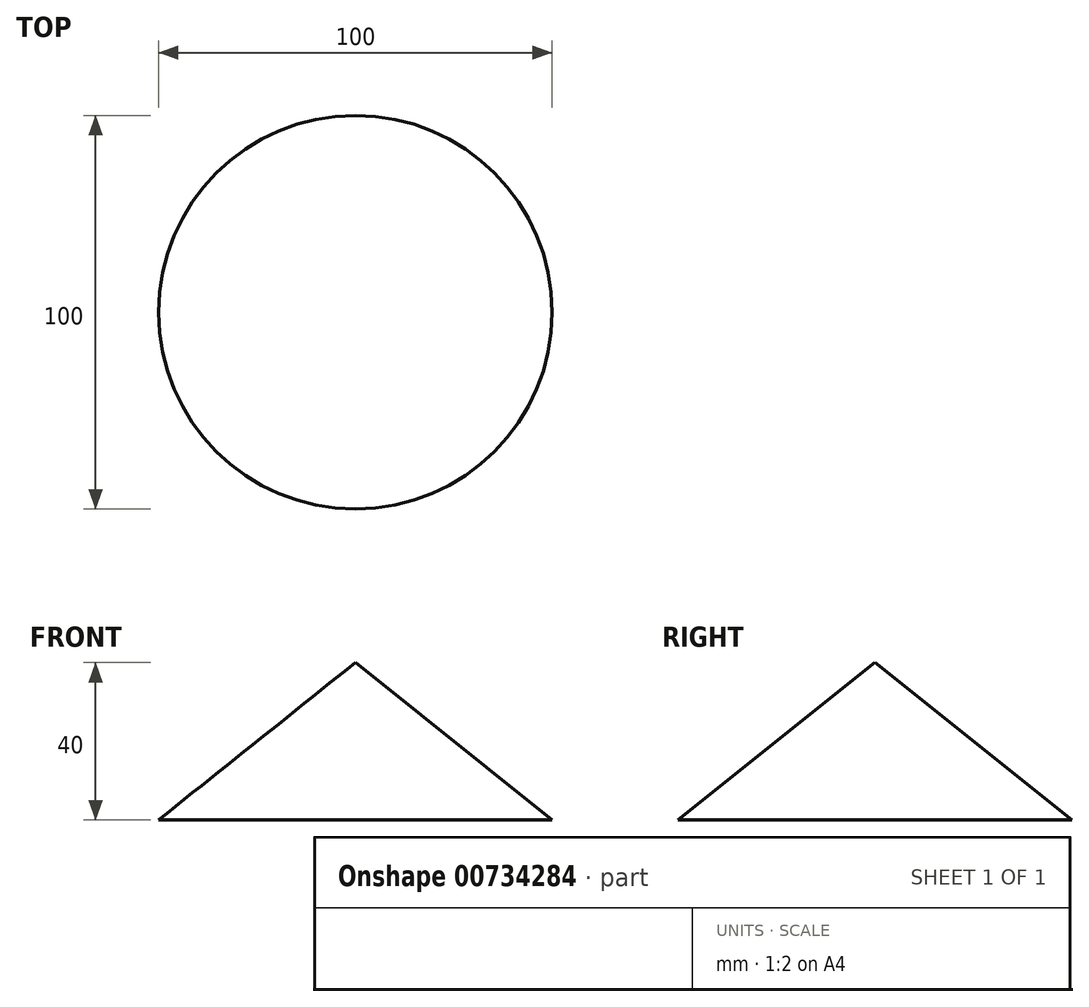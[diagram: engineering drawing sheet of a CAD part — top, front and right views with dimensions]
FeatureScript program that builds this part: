
annotation { "Feature Type Name" : "Feature", "Feature Type Description" : "" }
export const myFeature = defineFeature(function(context is Context, id is Id, definition is map)
    precondition{}
    {
        {
            var Q0;
            Q0=qCreatedBy(makeId("Front.planeOp"),FACE);
            var sketch = newSketch(context, id + "F0", { "sketchPlane" : qUnion([Q0])});
            skLineSegment(sketch, "E0", {"start": v(0, 0) * mm, "end": v(0, 40) * mm});
            skLineSegment(sketch, "E1", {"start": v(0, 40) * mm, "end": v(50, 0) * mm});
            skLineSegment(sketch, "E2", {"start": v(50, 0) * mm, "end": v(0, 0) * mm});
            skSolve(sketch);
        }
        {
            var Q0;
            Q0 = qSketchRegion(id + "F0", true);
            var Q1;
            Q1=makeQuery(id+"F0.imprint","IMPRINT",FACE,{"disambiguationData":[TD([[makeQuery(id+"F0.imprint","IMPRINT",EDGE,{"derivedFrom":sQuery(id+"F0.wireOp",EDGE,"E0")}),-1.0]])]});
            var Q2;
            Q2=sQuery(id+"F0.wireOp",EDGE,"E0");
            revolve(context, id + "F1", {"surfaceOperationType" : NewSurfaceOperationType.NEW, "entities" : qUnion([Q0, Q1]), "axis" : qUnion([Q2]), "revolveType" : RevolveType.FULL});
        }
    });
